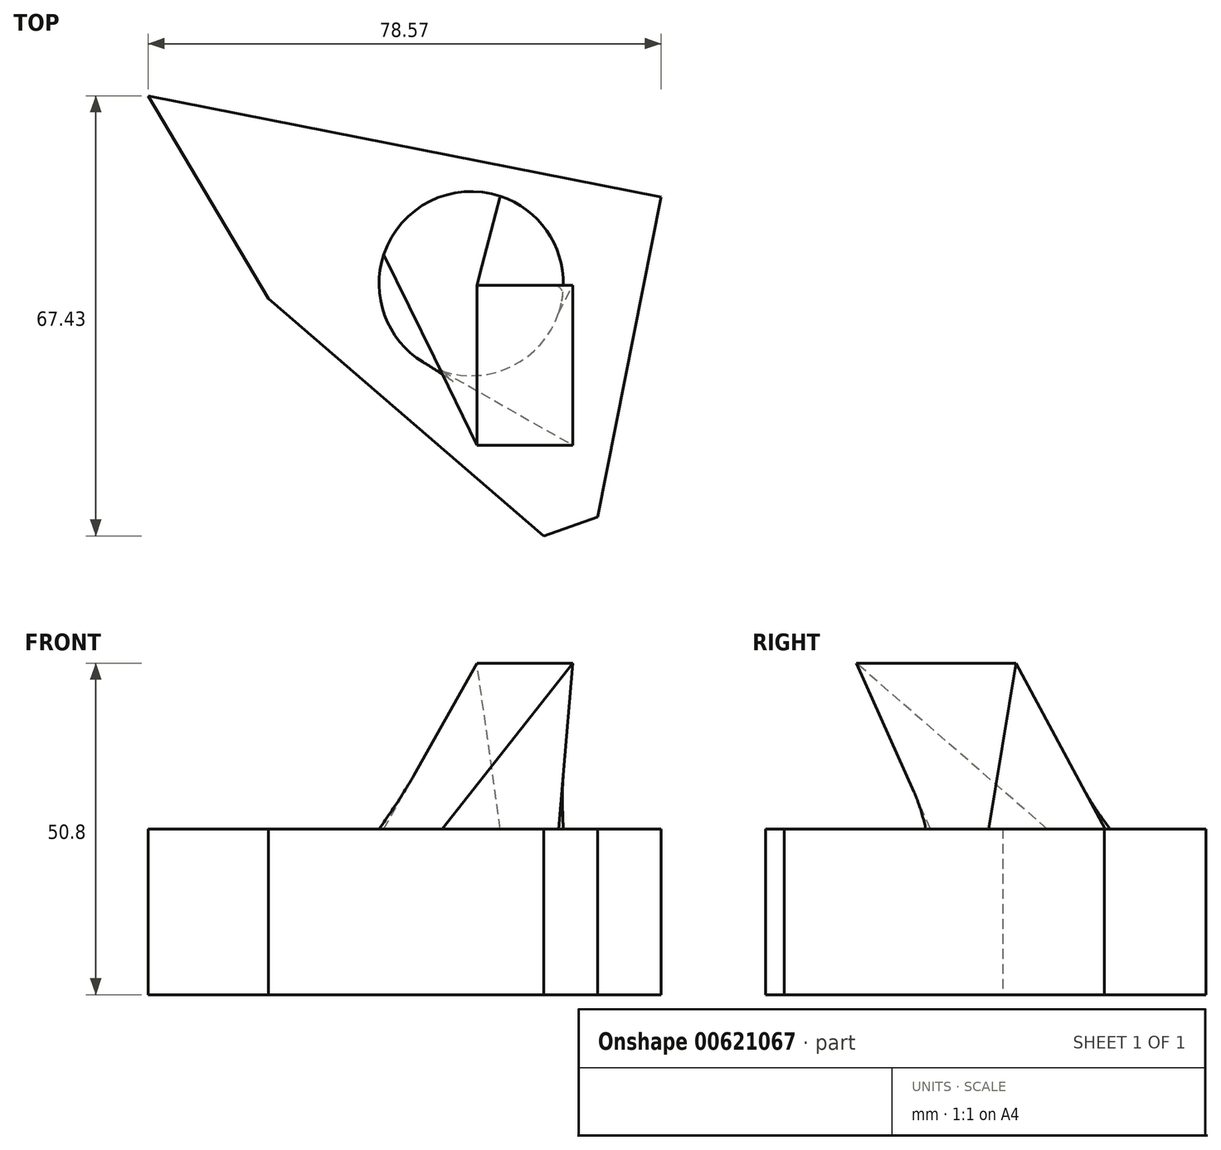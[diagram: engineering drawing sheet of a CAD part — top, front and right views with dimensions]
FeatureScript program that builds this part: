
annotation { "Feature Type Name" : "Feature", "Feature Type Description" : "" }
export const myFeature = defineFeature(function(context is Context, id is Id, definition is map)
    precondition{}
    {
        {
            var Q0;
            Q0=qCreatedBy(makeId("Top.planeOp"),FACE);
            var sketch = newSketch(context, id + "F0", { "sketchPlane" : qUnion([Q0])});
            skLineSegment(sketch, "E0", {"start": v(-34.4, 37.27) * mm, "end": v(44.18, 21.73) * mm});
            skLineSegment(sketch, "E1", {"start": v(44.18, 21.73) * mm, "end": v(32.79, -35.86) * mm});
            skLineSegment(sketch, "E2", {"start": v(32.79, -35.86) * mm, "end": v(-15.97, 6.19) * mm});
            skLineSegment(sketch, "E3", {"start": v(-15.97, 6.19) * mm, "end": v(-34.4, 37.27) * mm});
            skSolve(sketch);
        }
        {
            var Q0;
            Q0 = qSketchRegion(id + "F0", true);
            extrude(context, id + "F1", {"entities" : qUnion([Q0]), "depth" : 25.4 * mm, "offsetDistance" : 25.4 * mm});
        }
        {
            var Q0;
            Q0=makeQuery(id+"F1.opExtrude","SWEPT_EDGE",EDGE,{"disambiguationData":[OSD([sQuery(id+"F0.wireOp",EDGE,"E1"),sQuery(id+"F0.wireOp",EDGE,"E2")])]});
            chamfer(context, id + "F2", {"entities" : qUnion([Q0]), "width" : 5.08 * mm, "tangentPropagation" : true});
        }
        {
            var Q0;
            Q0=makeQuery(id+"F1.opExtrude","CAP_FACE",FACE,{"disambiguationData":[OSD([sQuery(id+"F0.wireOp",EDGE,"E0"),sQuery(id+"F0.wireOp",EDGE,"E1"),sQuery(id+"F0.wireOp",EDGE,"E2"),sQuery(id+"F0.wireOp",EDGE,"E3")])],"isStart":false});
            var sketch = newSketch(context, id + "F3", { "sketchPlane" : qUnion([Q0])});
            skCircle(sketch, "E4", {"center": v(15.1, 8.5) * mm, "radius": 14.11 * mm});
            skSolve(sketch);
        }
        {
            var Q0;
            Q0=makeQuery(id+"F3.imprint","IMPRINT",FACE,{"disambiguationData":[TD([[makeQuery(id+"F3.imprint","IMPRINT",EDGE,{"derivedFrom":sQuery(id+"F3.wireOp",EDGE,"E4")}),-1.0]])]});
            cPlane(context, id + "F4", {"entities" : qUnion([Q0]), "cplaneType" : CPlaneType.OFFSET, "offset" : 25.4 * mm, "width" : 152.4 * mm, "height" : 152.4 * mm});
        }
        {
            var Q0;
            Q0=qCreatedBy(id+"F4.planeOp",FACE);
            var sketch = newSketch(context, id + "F5", { "sketchPlane" : qUnion([Q0])});
            skLineSegment(sketch, "E5.bottom", {"start": v(15.97, 8.2) * mm, "end": v(30.65, 8.2) * mm});
            skLineSegment(sketch, "E5.top", {"start": v(15.97, -16.26) * mm, "end": v(30.65, -16.26) * mm});
            skLineSegment(sketch, "E5.left", {"start": v(15.97, 8.2) * mm, "end": v(15.97, -16.26) * mm});
            skLineSegment(sketch, "E5.right", {"start": v(30.65, 8.2) * mm, "end": v(30.65, -16.26) * mm});
            skSolve(sketch);
        }
        {
            var Q1;
            Q1=makeQuery(id+"F3.imprint","IMPRINT",FACE,{"disambiguationData":[TD([[makeQuery(id+"F3.imprint","IMPRINT",EDGE,{"derivedFrom":sQuery(id+"F3.wireOp",EDGE,"E4")}),1.0]])]});
            var Q2;
            Q2=makeQuery(id+"F5.imprint","IMPRINT",FACE,{"disambiguationData":[TD([[makeQuery(id+"F5.imprint","IMPRINT",EDGE,{"derivedFrom":sQuery(id+"F5.wireOp",EDGE,"E5.bottom")}),-1.0]])]});
            loft(context, id + "F6", {"operationType" : NewBodyOperationType.ADD, "sheetProfilesArray" : [{ "sheetProfileEntities" : qUnion([Q1]) }, { "sheetProfileEntities" : qUnion([Q2]) }]});
        }
    });
